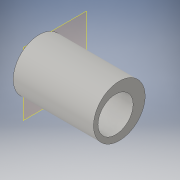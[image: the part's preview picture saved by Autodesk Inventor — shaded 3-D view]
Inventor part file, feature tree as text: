
AUTODESK INVENTOR PART (.ipt)
format: ipt  version: 2016 (Build 200138000, 138)  size: 96,768 bytes
history: native  units: in
note: dims shown in document units (in); Inventor stores cm internally (conversion verified against a paired STEP export)
features: plane x1, extrude x1, hole x1, sketch x1
ambient origin geometry x8: Origin, YZ Plane, XZ Plane, XY Plane, X Axis, Y Axis, Z Axis, Center Point
bodies: Solid1 (feature_tree)
feature tree (4):
  plane  "Work Plane1"
  extrude  "Extrusion1"  Depth=1.0in TaperAngle=0.0deg
  hole  "Hole1"  [1 undecoded]
  sketch  "Sketch1"  dims[d0=0.4375in d1=1.0in d2=0.0in d3=1.0in d4=1.0in d5=0.4375in d6=0.75in d7=0.375in d8=0.25in d9=0.5635in d10=1.0in d11=0.8108in]
note: 1 required parameter value undecoded (feature->parameter linkage not recoverable at this tier; creation-order binding heuristic only, values carry confidence <= 0.55)
